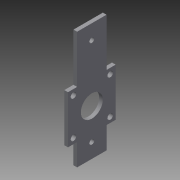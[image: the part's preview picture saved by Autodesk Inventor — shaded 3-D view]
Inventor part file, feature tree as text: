
AUTODESK INVENTOR PART (.ipt)
format: ipt  version: 2014 SP1 (Build 180222100, 222)  size: 109,568 bytes
history: native  units: in
note: dims shown in document units (in); Inventor stores cm internally (conversion verified against a paired STEP export)
features: extrude x1, sketch x1
ambient origin geometry x8: Origin, YZ Plane, XZ Plane, XY Plane, X Axis, Y Axis, Z Axis, Center Point
bodies: Solid1 (feature_tree)
feature tree (2):
  extrude  "Extrusion1"  Depth=4.0in
  sketch  "Sketch1"  dims[d0=1.0in d1=4.0in d2=1.625in d3=1.625in d5=0.164in d6=0.164in d7=1.25in d8=1.25in d10=0.1875in d11=0.5in d12=0.5in d13=0.5in d15=0.188in d16=0.7874in d18=1.25in d19=0.7874in d21=1.25in d24=0.75in d25=0.8125in d26=0.8125in d27=0.125in d28=0.0in d29=2.44in d30=0.1875in d31=0.5in]
